# Revit family: Accessory-Storage_Tray-KOHLER-K-33464
name_source: partatom
category: Specialty Equipment
units: mm (PartAtom-declared; Revit-internal decimal feet)

## family parameters
Cut with Voids When Loaded = No
Host = Face
OmniClass Number = 23.31.25.00
OmniClass Title = Toilet and Bath Specialties
Part Type = Normal
Room Calculation Point = No
Round Connector Dimension = Use Diameter
Shared = No

## types (1)
- 58-Thunder Grey
    ADA Compliant = No
    Assembly Code = C1030200
    Date Modified = 02/28/2024
    Default Elevation = 42"
    Description = Storage Tray
    Finish = Kohler-Plastic-58-Thunder_Grey
    Height = 4 5/16"
    Length = 4"
    Manufacturer = Kohler Co.
    Master Format 2014 = 10 28 00
    Master Format 2014 Name = Toilet, Bath, and Laundry Accessories
    Material = Plastic
    Model = K-33464-58
    Product Documentation Link = https://www.us.kohler.com
    Product Name = Deep
    Product Page URL = http://www.us.kohler.com
    Type = 1
    URL = https://www.us.kohler.com
    WaterSense Certified = No
    Width = 21 1/2"

## geometry (parser evidence)
native form markers: Sweep x5
no freeform markers — native parametric forms only
